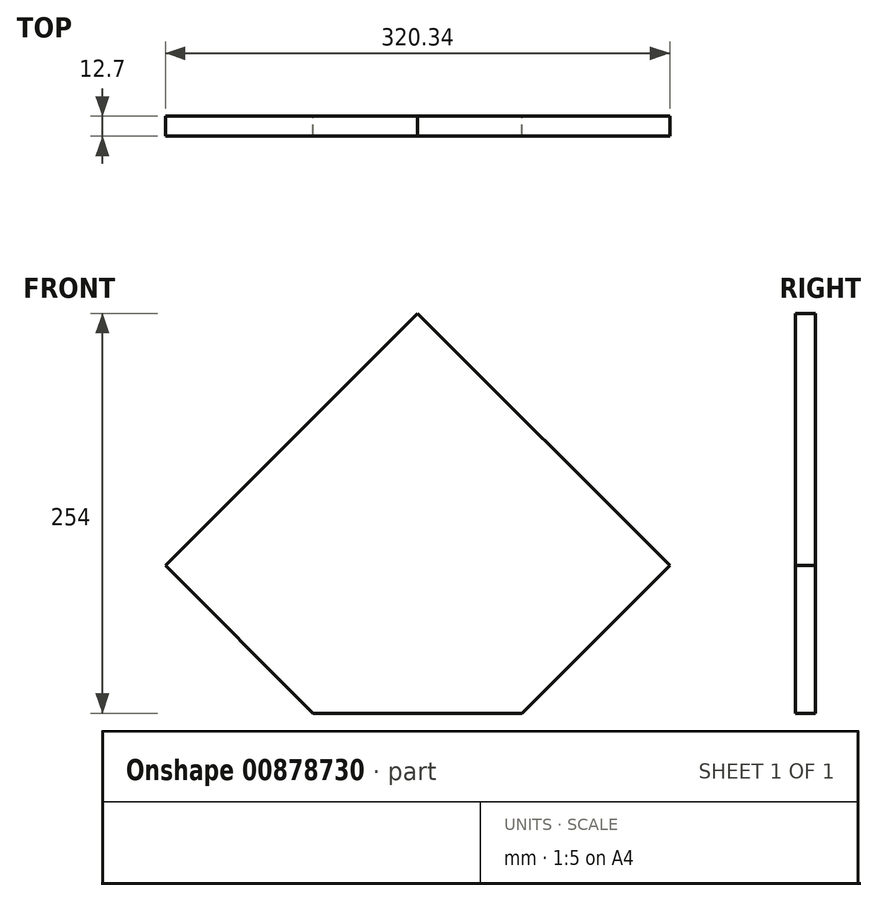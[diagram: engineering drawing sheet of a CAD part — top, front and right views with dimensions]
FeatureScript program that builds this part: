
annotation { "Feature Type Name" : "Feature", "Feature Type Description" : "" }
export const myFeature = defineFeature(function(context is Context, id is Id, definition is map)
    precondition{}
    {
        {
            var Q0;
            Q0=qCreatedBy(makeId("Front.planeOp"),FACE);
            var sketch = newSketch(context, id + "F0", { "sketchPlane" : qUnion([Q0])});
            skLineSegment(sketch, "E0", {"start": v(-66.35, 0) * mm, "end": v(-160.17, 93.83) * mm});
            skLineSegment(sketch, "E1", {"start": v(-160.17, 93.83) * mm, "end": v(0, 254) * mm});
            skLineSegment(sketch, "E2", {"start": v(0, 254) * mm, "end": v(160.17, 93.83) * mm});
            skLineSegment(sketch, "E3", {"start": v(160.17, 93.83) * mm, "end": v(66.35, 0) * mm});
            skLineSegment(sketch, "E4", {"start": v(66.35, 0) * mm, "end": v(-66.35, 0) * mm});
            skSolve(sketch);
        }
        {
            var Q0;
            Q0=makeQuery(id+"F0.imprint","IMPRINT",FACE,{"disambiguationData":[TD([[makeQuery(id+"F0.imprint","IMPRINT",EDGE,{"derivedFrom":sQuery(id+"F0.wireOp",EDGE,"E0")}),-1.0]])]});
            extrude(context, id + "F1", {"entities" : qUnion([Q0]), "depth" : 12.7 * mm, "offsetDistance" : 25.4 * mm});
        }
    });
